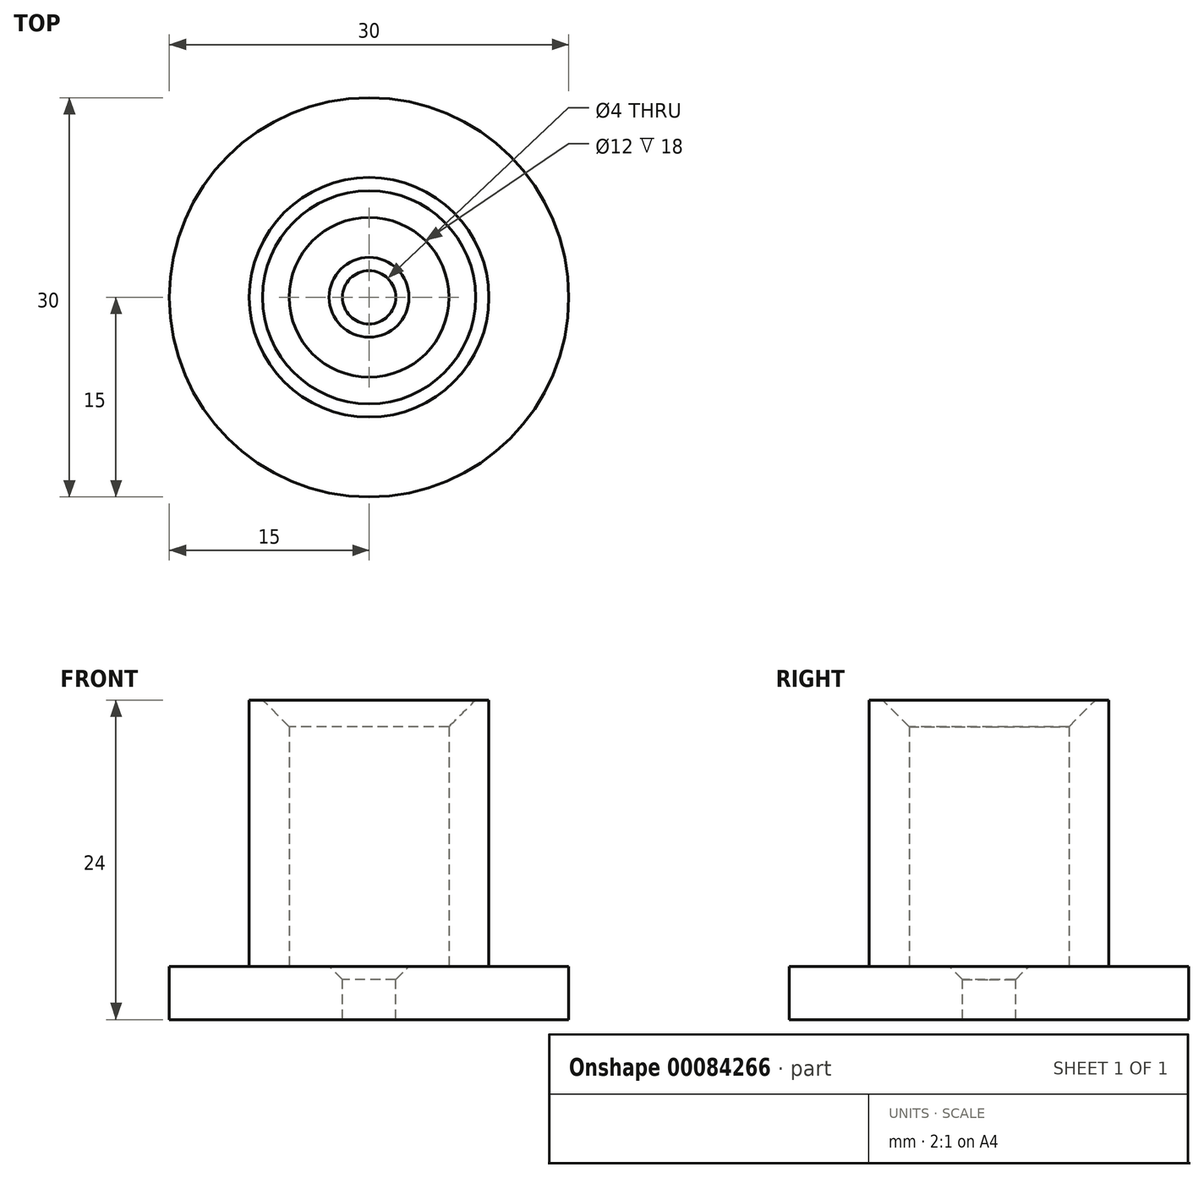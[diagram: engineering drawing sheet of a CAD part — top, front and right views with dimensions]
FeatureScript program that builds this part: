
annotation { "Feature Type Name" : "Feature", "Feature Type Description" : "" }
export const myFeature = defineFeature(function(context is Context, id is Id, definition is map)
    precondition{}
    {
        {
            var Q0;
            Q0=qCreatedBy(makeId("Top.planeOp"),FACE);
            var sketch = newSketch(context, id + "F0", { "sketchPlane" : qUnion([Q0])});
            skCircle(sketch, "E0", {"center": v(0, 0) * mm, "radius": 6 * mm});
            skCircle(sketch, "E1", {"center": v(0, 0) * mm, "radius": 9 * mm});
            skCircle(sketch, "E2", {"center": v(0, 0) * mm, "radius": 2 * mm});
            skCircle(sketch, "E3", {"center": v(0, 0) * mm, "radius": 15 * mm});
            skSolve(sketch);
        }
        {
            var Q0;
            Q0=makeQuery(id+"F0.imprint","IMPRINT",FACE,{"disambiguationData":[TD([[makeQuery(id+"F0.imprint","IMPRINT",EDGE,{"derivedFrom":sQuery(id+"F0.wireOp",EDGE,"E0")}),1.0]])]});
            var Q1;
            Q1=makeQuery(id+"F0.imprint","IMPRINT",FACE,{"disambiguationData":[TD([[makeQuery(id+"F0.imprint","IMPRINT",EDGE,{"derivedFrom":sQuery(id+"F0.wireOp",EDGE,"E0")}),-1.0]])]});
            var Q2;
            Q2=makeQuery(id+"F0.imprint","IMPRINT",FACE,{"disambiguationData":[TD([[makeQuery(id+"F0.imprint","IMPRINT",EDGE,{"derivedFrom":sQuery(id+"F0.wireOp",EDGE,"E1")}),-1.0]])]});
            extrude(context, id + "F1", {"entities" : qUnion([Q0, Q1, Q2]), "oppositeDirection" : true, "depth" : 4 * mm});
        }
        {
            var Q0;
            Q0=makeQuery(id+"F0.imprint","IMPRINT",FACE,{"disambiguationData":[TD([[makeQuery(id+"F0.imprint","IMPRINT",EDGE,{"derivedFrom":sQuery(id+"F0.wireOp",EDGE,"E0")}),-1.0]])]});
            extrude(context, id + "F2", {"entities" : qUnion([Q0]), "operationType" : NewBodyOperationType.ADD, "depth" : 20 * mm});
        }
        {
            var Q0;
            Q0=makeQuery(id+"F1.opExtrude","CAP_EDGE",EDGE,{"disambiguationData":[OSD([sQuery(id+"F0.wireOp",EDGE,"E2")])],"isStart":true});
            chamfer(context, id + "F3", {"entities" : qUnion([Q0]), "width" : 1 * mm, "tangentPropagation" : true});
        }
        {
            var Q0;
            Q0=makeQuery(id+"F2.opExtrude","CAP_EDGE",EDGE,{"disambiguationData":[OSD([sQuery(id+"F0.wireOp",EDGE,"E0")])],"isStart":false});
            chamfer(context, id + "F4", {"entities" : qUnion([Q0]), "width" : 2 * mm, "tangentPropagation" : true});
        }
    });
